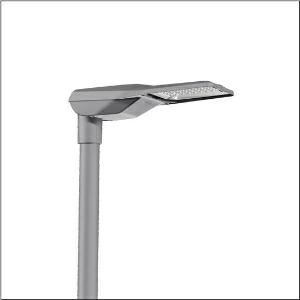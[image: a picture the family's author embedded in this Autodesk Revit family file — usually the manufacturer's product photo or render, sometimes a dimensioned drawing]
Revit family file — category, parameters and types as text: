
# Revit family: streetlight_sl_21_iq_mini___st0_8a_5xe2c41d08gb_f485
name_source: partatom
category: Lighting Fixtures
units: mm (PartAtom-declared; Revit-internal decimal feet)

## family parameters
Cut with Voids When Loaded = No
Host = Face
Light Source = No
Part Type = Normal
Room Calculation Point = No
Round Connector Dimension = Use Diameter
Shared = No

## types (1)
- --- (1 x LED, 5920 lm, 37.1 W, 4000K)
    Apparent Load = 37 VA
    CIE Flux Codes = 38 75 97 100 100
    Color Rendering = 70
    Color Temperature = 4000K
    Default Elevation = 1800 mm
    Description = Streetlight SL 21 iQ mini, mast luminaire, primary light control with lens, of PMMA, primary optical cover: cover, of toughened safety glass, transparent, light distribution: ST0.8a, light emission: direct distribution, primary light characteristic: asymmetric, installation type: post-top, side-entry, LED, High Power LED, rated luminous flux: 5.920lm, luminous efficacy: 160lm/W, light colour: 740, colour temperature: 4000K, control: Auto-Match, Temp-Guard, Lumen-Switch, Night-Set, Smart-Wire, Light-Fading, Desk-Remote (wireless, voltage-free reading and setting of iQ features in the workshop via application-optimized NFC function/RFID function), optimised constant luminous flux control (CLO 2.0), presetting dimming linear, mains connection: 220..240V, AC, 50/60Hz, start of lifetime: 37W, end of service life: 39W, reduction: 18W, luminaire housing, of diecast aluminium, powder-coated, Siteco® metallic grey (DB 702S), corrosivity category C5 mid according to DIN EN ISO 12944, please order mast flange separately, inclination adjustable: 0°, 5°, 10°, 15°, sealing non-destructively replaceable, multi-level sealing system, length: 628mm, width: 235mm, height: 110mm, mast flange for spigot size: 42mm (side-entry): 5XC10008XM4, 60/48mm (side-entry/post-top): 5XC10108XM2, 76/60mm (side-entry/post-top): 5XC10108XM1, protection rating (complete): IP66, insulation class (complete): insulation class II (safety insulation), certification: CE, ENEC, ENEC+, VDE, impact resistance: IK09, permissible operating ambient temperature for outdoor applications: -40..+50°C, standard-compliant lighting for roads and squares, packaging unit: 1 piece

Light Distribution: ST0.8a
    Height = 110 mm
    Lamp = 1 x LED
    Lamp Light Flux = 5920 lm
    Lamp Power = 37.1 W
    Lamp count = 1
    Length = 625 mm
    Luminous efficacy = 160 lm/W
    Manufacturer = Siteco
    ModVariant = No
    Model = 5XE2C41D08GB
    Number of Poles = 1
    OnlyDefault = Yes
    Power Factor = 1
    Product Name = Streetlight SL 21 iQ mini | ST0.8a
    Product group = mast luminaire | pylon top
    ProductGroupID = 6100
    Protection Class = Protection class II
    Protection Degree = IP 66
    RLX_Detail_Level = 1
    RLX_Emergency_Light_Flux = 0 lm
    RLX_Emergency_Type = 0
    RLX_Emergency_Type_DB = No
    RlxData = <blob elided: 92009 chars, md5=6f14067c>
    Socket = socket
    Standby Power = 0 W
    System Light Flux = 5920 lm
    System Power = 37 W
    Type Comments = factory setting: luminous flux: 100 % | dim-lin: 254 | 385 mA
    Type Image = l_1003519.jpg
    URL = http://relux.com
    VarID = @adj_137243
    Voltage = 0 V
    Weight = 0.00 kg
    Width = 234 mm

## geometry (parser evidence)
native form markers: Blend x4, Sweep x10
no freeform markers — native parametric forms only
